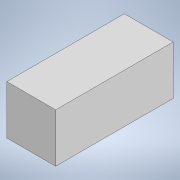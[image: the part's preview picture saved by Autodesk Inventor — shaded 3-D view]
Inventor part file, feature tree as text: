
AUTODESK INVENTOR PART (.ipt)
format: ipt  version: 2020 (Build 240168000, 168)  size: 85,504 bytes
history: native  units: in
note: dims shown in document units (in); Inventor stores cm internally (conversion verified against a paired STEP export)
features: extrude x1, sketch x1
ambient origin geometry x8: Origin, YZ Plane, XZ Plane, XY Plane, X Axis, Y Axis, Z Axis, Center Point
bodies: Solid1 (feature_tree)
feature tree (2):
  extrude  "Extrusion1"  Depth=1.9685in
  sketch  "Sketch1"  dims[d0=1.9685in d1=1.9685in d2=4.7318in d3=0.0in]
